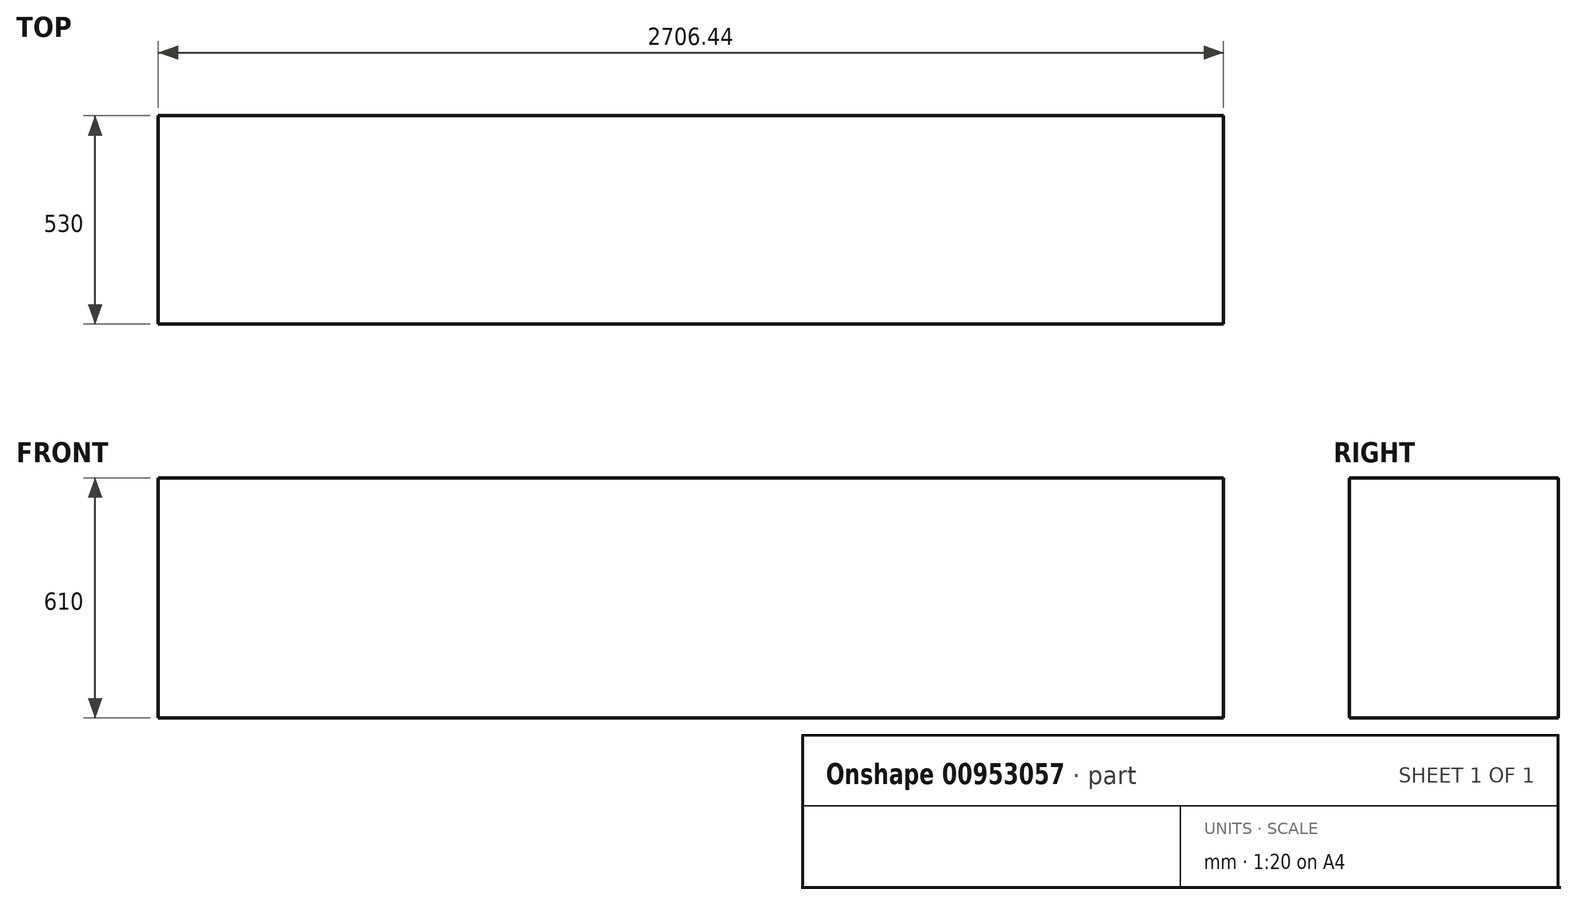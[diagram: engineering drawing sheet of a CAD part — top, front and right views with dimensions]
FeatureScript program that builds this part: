
annotation { "Feature Type Name" : "Feature", "Feature Type Description" : "" }
export const myFeature = defineFeature(function(context is Context, id is Id, definition is map)
    precondition{}
    {
        {
            var Q0;
            Q0=qCreatedBy(makeId("Front.planeOp"),FACE);
            var sketch = newSketch(context, id + "F0", { "sketchPlane" : qUnion([Q0])});
            skLineSegment(sketch, "E0.bottom", {"start": v(-1350.3, -336.68) * mm, "end": v(1356.15, -336.68) * mm});
            skLineSegment(sketch, "E0.top", {"start": v(-1350.3, 258.32) * mm, "end": v(1356.15, 258.32) * mm});
            skLineSegment(sketch, "E0.left", {"start": v(-1350.3, -336.68) * mm, "end": v(-1350.3, 258.32) * mm});
            skLineSegment(sketch, "E0.right", {"start": v(1356.15, -336.68) * mm, "end": v(1356.15, 258.32) * mm});
            skSolve(sketch);
        }
        {
            var Q0;
            Q0 = qSketchRegion(id + "F0", true);
            extrude(context, id + "F1", {"entities" : qUnion([Q0]), "depth" : 530 * mm, "offsetDistance" : 25 * mm});
        }
        {
            var Q0;
            Q0=makeQuery(id+"F1.opExtrude","SWEPT_FACE",FACE,{"disambiguationData":[OSD([sQuery(id+"F0.wireOp",EDGE,"E0.top")])]});
            var sketch = newSketch(context, id + "F2", { "sketchPlane" : qUnion([Q0])});
            skSolve(sketch);
        }
        {
            var Q0;
            {var subQ0=sQuery(id+"F0.wireOp",EDGE,"E0.top");Q0=makeQuery(id+"F2.imprint","IMPRINT",FACE,{"disambiguationData":[TD([[makeQuery(id+"F2.imprint","IMPRINT",EDGE,{"derivedFrom":makeQuery(id+"F1.opExtrude","CAP_EDGE",EDGE,{"disambiguationData":[OSD([subQ0])],"isStart":true})}),-1.0]])]});}
            extrude(context, id + "F3", {"entities" : qUnion([Q0]), "operationType" : NewBodyOperationType.ADD, "depth" : 15 * mm, "offsetDistance" : 25 * mm});
        }
    });
